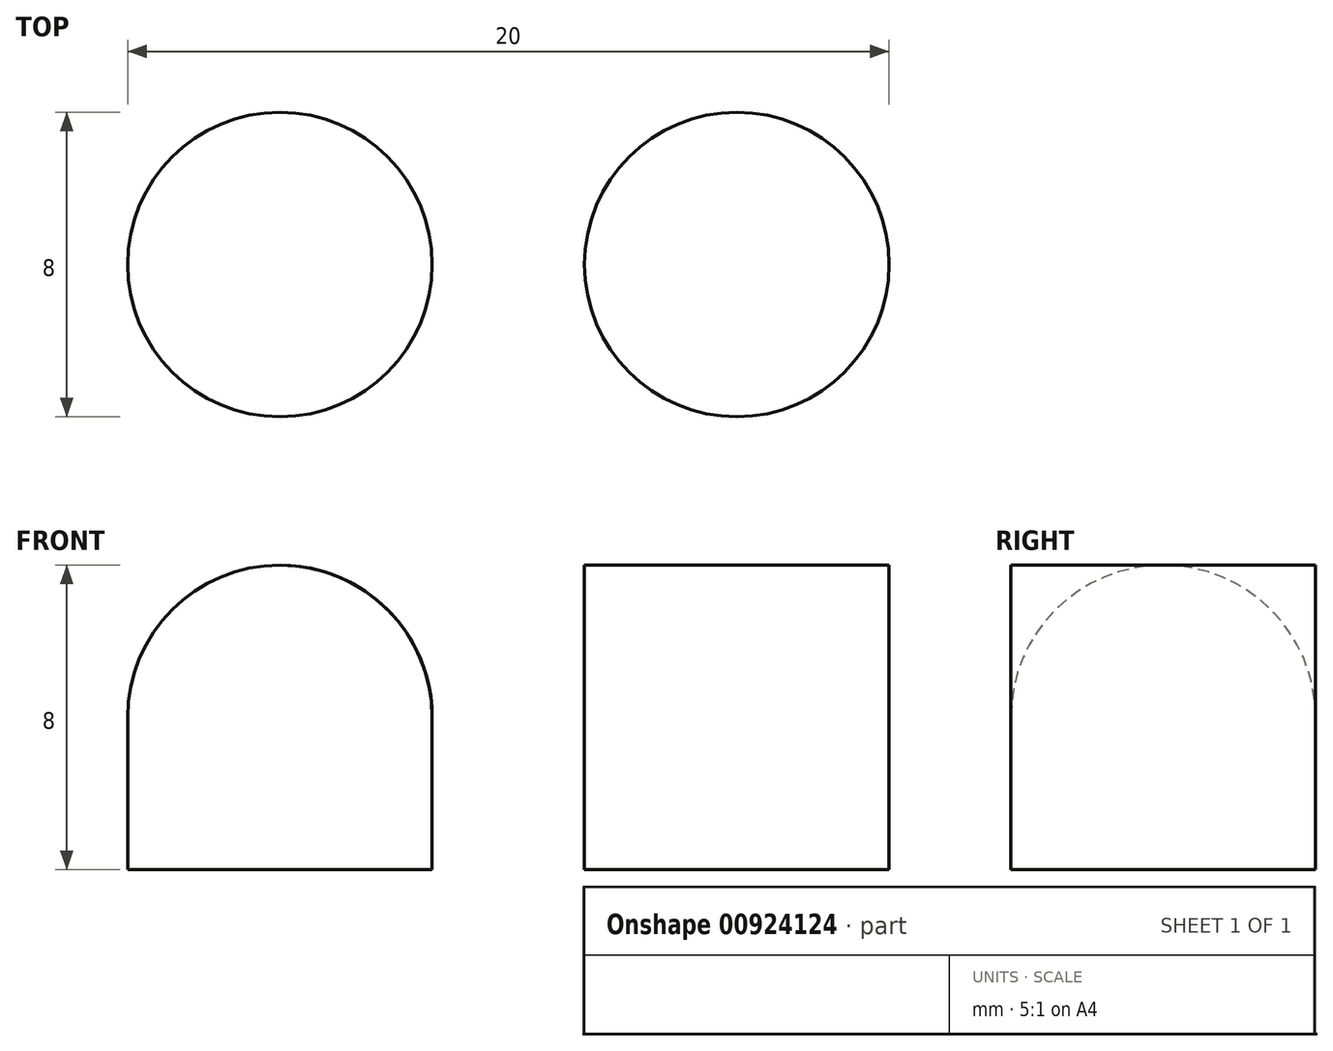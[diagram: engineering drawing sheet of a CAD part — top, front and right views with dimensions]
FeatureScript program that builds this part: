
annotation { "Feature Type Name" : "Feature", "Feature Type Description" : "" }
export const myFeature = defineFeature(function(context is Context, id is Id, definition is map)
    precondition{}
    {
        {
            var Q0;
            Q0=qCreatedBy(makeId("Top.planeOp"),FACE);
            var sketch = newSketch(context, id + "F0", { "sketchPlane" : qUnion([Q0])});
            skCircle(sketch, "E0", {"center": v(0, 0) * mm, "radius": 4 * mm});
            skSolve(sketch);
        }
        {
            var Q0;
            Q0 = qSketchRegion(id + "F0", true);
            extrude(context, id + "F1", {"entities" : qUnion([Q0]), "depth" : 8 * mm, "offsetDistance" : 25 * mm});
        }
        {
            var Q0;
            Q0=qCreatedBy(makeId("Front.planeOp"),FACE);
            var sketch = newSketch(context, id + "F2", { "sketchPlane" : qUnion([Q0])});
            skLineSegment(sketch, "E1", {"start": v(-12, 0) * mm, "end": v(-12, 8) * mm});
            skLineSegment(sketch, "E2", {"start": v(-8, 0) * mm, "end": v(-8, 4) * mm});
            skArc(sketch, "E3", {"start": v(-8, 4) * mm, "mid": v(-11.86, 8) * mm, "end": v(-16, 4.27) * mm});
            skLineSegment(sketch, "E4", {"start": v(-12, 0) * mm, "end": v(-8, 0) * mm});
            skSolve(sketch);
        }
        {
            var Q0;
            {var subQ0=sQuery(id+"F2.wireOp",EDGE,"E1");Q0=makeQuery(id+"F2.imprint","IMPRINT",FACE,{"disambiguationData":[TD([[makeQuery(id+"F2.imprint","IMPRINT",EDGE,{"derivedFrom":subQ0}),-1.0]])]});}
            var Q1;
            Q1=sQuery(id+"F2.wireOp",EDGE,"E1");
            revolve(context, id + "F3", {"surfaceOperationType" : NewSurfaceOperationType.NEW, "entities" : qUnion([Q0]), "axis" : qUnion([Q1]), "revolveType" : RevolveType.FULL});
        }
    });
